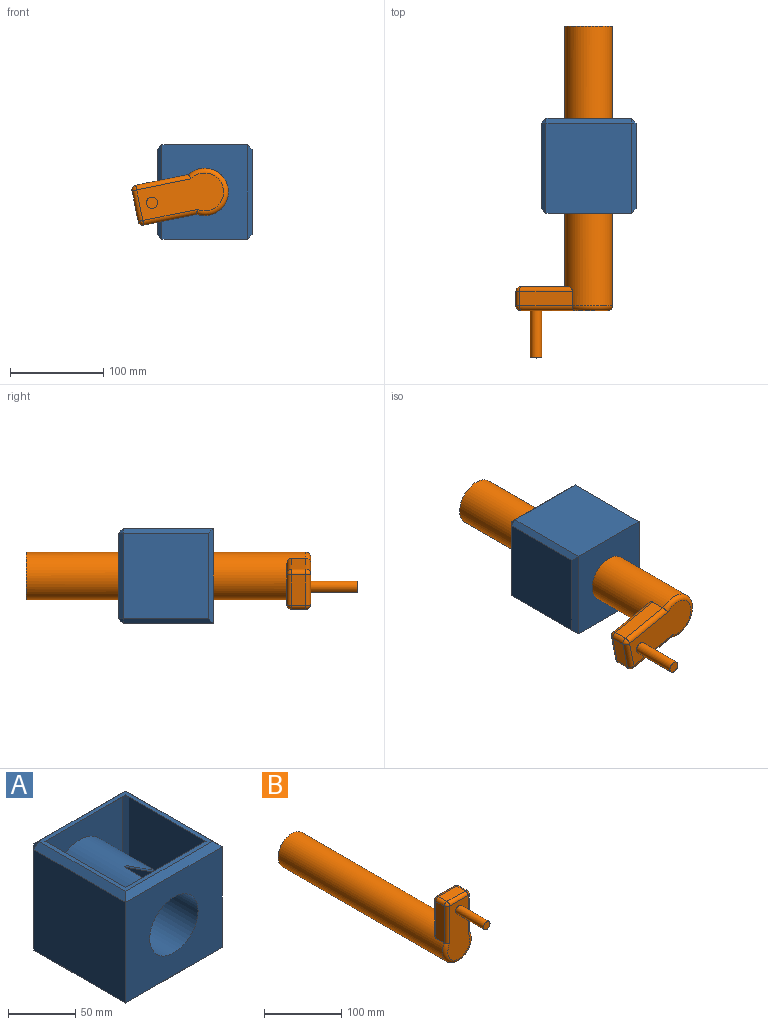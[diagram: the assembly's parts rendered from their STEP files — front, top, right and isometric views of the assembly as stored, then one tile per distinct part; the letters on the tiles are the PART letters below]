
ASSEMBLY  parts=2 mates=1
PART A: 44 faces, bbox 101.6x101.6x101.6 mm
  f0: cylinder r=27.94mm len=96.52mm, axis (0,-1,0), area 16821.6mm2, adj f25,f26,f41,f42,f43
  f1: plane 91.44x91.44mm, normal (0,0,1), area 1262.2mm2, adj f8,f9,f11,f12,f27,f28,f30,f31
  f2: plane 96.52x91.44mm, normal (-1,0,0), area 8825.8mm2, adj f5,f8,f13,f16
  f3: plane 91.44x91.44mm, normal (0,0,-1), area 8361.3mm2, adj f16,f18,f19,f21
  f4: plane 96.52x91.44mm, normal (1,0,0), area 8825.8mm2, adj f5,f11,f17,f21
  f5: plane 101.6x91.44mm, normal (0,-1,0), area 7263.5mm2, adj f2,f4,f7,f9,f19
  f6: plane 91.44x91.44mm, normal (0,1,0), area 6334.4mm2, adj f7,f12,f13,f17,f18
  f7: cylinder r=25.4mm len=101.6mm, axis (0,-1,0), area 16214.6mm2, adj f5,f6
  f8: plane 96.52x5.08mm, normal (-0.71,0,0.71), area 675.2mm2, adj f1,f2,f9,f10
  f9: plane 101.6x5.08mm, normal (0,-0.71,0.71), area 693.4mm2, adj f1,f5,f8,f11
  f10: plane 5.08x5.08mm, normal (-0.58,0.58,0.58), area 22.3mm2, adj f8,f12,f13
  f11: plane 96.52x5.08mm, normal (0.71,0,0.71), area 675.2mm2, adj f1,f4,f9,f14
  f12: plane 91.44x5.08mm, normal (0,0.71,0.71), area 656.9mm2, adj f1,f6,f10,f14
  f13: plane 91.44x5.08mm, normal (-0.71,0.71,0), area 656.9mm2, adj f2,f6,f10,f15
  f14: plane 5.08x5.08mm, normal (0.58,0.58,0.58), area 22.3mm2, adj f11,f12,f17
  f15: plane 5.08x5.08mm, normal (-0.58,0.58,-0.58), area 22.3mm2, adj f13,f16,f18
  f16: plane 96.52x5.08mm, normal (-0.71,0,-0.71), area 675.2mm2, adj f2,f3,f15,f19
  f17: plane 91.44x5.08mm, normal (0.71,0.71,0), area 656.9mm2, adj f4,f6,f14,f20
  f18: plane 91.44x5.08mm, normal (0,0.71,-0.71), area 656.9mm2, adj f3,f6,f15,f20
  f19: plane 101.6x5.08mm, normal (0,-0.71,-0.71), area 693.4mm2, adj f3,f5,f16,f21
  f20: plane 5.08x5.08mm, normal (0.58,0.58,-0.58), area 22.3mm2, adj f17,f18,f21
  f21: plane 96.52x5.08mm, normal (0.71,0,-0.71), area 675.2mm2, adj f3,f4,f19,f20
  f22: plane 92.93x89.34mm, normal (1,0,0), area 8301.8mm2, adj f25,f27,f32,f35
  f23: plane 89.34x89.34mm, normal (0,0,1), area 7980.9mm2, adj f35,f37,f38,f40
  f24: plane 92.93x89.34mm, normal (-1,0,0), area 8301.8mm2, adj f25,f30,f36,f40
  f25: plane 96.52x89.34mm, normal (0,1,0), area 6127.7mm2, adj f0,f22,f24,f28,f38,f41,f42
  f26: plane 89.34x89.34mm, normal (0,-1,0), area 5528.4mm2, adj f0,f31,f32,f36,f37
  f27: plane 93.17x6.13mm, normal (0.71,0,-0.71), area 775.9mm2, adj f1,f22,f28,f29,f31,f32
  f28: plane 96.52x6.13mm, normal (0,0.71,-0.71), area 783.9mm2, adj f1,f25,f27,f30,f43
  f29: plane 3.1x3.1mm, normal (0.58,-0.58,-0.58), area 8.3mm2, adj f27,f31,f32
  f30: plane 93.17x6.13mm, normal (-0.71,0,-0.71), area 775.9mm2, adj f1,f24,f28,f31,f33,f36
  f31: plane 89.83x6.13mm, normal (0,-0.71,-0.71), area 767.9mm2, adj f1,f26,f27,f29,f30,f32,f33,f36
  f32: plane 89.83x3.59mm, normal (0.71,-0.71,0), area 456.1mm2, adj f22,f26,f27,f29,f31,f34,f35,f37
  f33: plane 3.1x3.1mm, normal (-0.58,-0.58,-0.58), area 8.3mm2, adj f30,f31,f36
  f34: plane 3.1x3.1mm, normal (0.58,-0.58,0.58), area 8.3mm2, adj f32,f35,f37
  f35: plane 93.17x3.59mm, normal (0.71,0,0.71), area 464.1mm2, adj f22,f23,f32,f34,f37,f38
  f36: plane 89.83x3.59mm, normal (-0.71,-0.71,0), area 456.1mm2, adj f24,f26,f30,f31,f33,f37,f39,f40
  f37: plane 89.83x3.59mm, normal (0,-0.71,0.71), area 456.1mm2, adj f23,f26,f32,f34,f35,f36,f39,f40
  f38: plane 96.52x3.59mm, normal (0,0.71,0.71), area 472.1mm2, adj f23,f25,f35,f40
  f39: plane 3.1x3.1mm, normal (-0.58,-0.58,0.58), area 8.3mm2, adj f36,f37,f40
  f40: plane 93.17x3.59mm, normal (-0.71,0,0.71), area 464.1mm2, adj f23,f24,f36,f37,f38,f39
  f41: plane 48.34x16.76mm, normal (1,0,0), area 405mm2, adj f0,f25,f43
  f42: plane 48.34x16.76mm, normal (-1,0,0), area 405mm2, adj f0,f25,f43
  f43: plane 48.34x16.76mm, normal (0,0.33,0.94), area 129.8mm2, adj f0,f28,f41,f42
PART B: 22 faces, bbox 55x355.6x103.5 mm
  f0: cylinder r=25.4mm len=299.72mm, axis (0,1,0), area 46788.4mm2, adj f2,f3,f4,f5,f7,f10,f18
  f1: plane 91.29x40.64mm, normal (0,-1,0), area 2961.7mm2, adj f14,f16,f18,f19,f20
  f2: plane 50.8x50.8mm, normal (0,1,0), area 2026.8mm2, adj f0
  f3: plane 57.91x15.24mm, normal (1,0,0), area 882.6mm2, adj f0,f10,f15,f19
  f4: plane 51.84x33.41mm, normal (0,1,0), area 1588.6mm2, adj f0,f7,f9,f10
  f5: plane 57.91x15.24mm, normal (-1,0,0), area 882.6mm2, adj f0,f7,f11,f16
  f6: plane 33.41x15.24mm, normal (0,0,1), area 509.2mm2, adj f9,f11,f14,f15
  f7: cylinder r=5.08mm len=57.91mm, axis (0,0,1), area 442.3mm2, adj f0,f4,f5,f8
  f8: sphere r=5.08mm, area 40.5mm2, adj f7,f9,f11
  f9: cylinder r=5.08mm len=33.41mm, axis (-1,0,0), area 266.6mm2, adj f4,f6,f8,f12
  f10: cylinder r=5.08mm len=57.91mm, axis (0,0,-1), area 442.3mm2, adj f0,f3,f4,f12
  f11: cylinder r=5.08mm len=15.24mm, axis (0,-1,0), area 121.6mm2, adj f5,f6,f8,f13
  f12: sphere r=5.08mm, area 40.5mm2, adj f9,f10,f15
  f13: sphere r=5.08mm, area 40.5mm2, adj f11,f14,f16
  f14: cylinder r=5.08mm len=33.41mm, axis (-1,0,0), area 266.6mm2, adj f1,f6,f13,f17
  f15: cylinder r=5.08mm len=15.24mm, axis (0,1,0), area 121.6mm2, adj f3,f6,f12,f17
  f16: cylinder r=5.08mm len=59.4mm, axis (0,0,1), area 466.3mm2, adj f1,f5,f13,f18
  f17: sphere r=5.08mm, area 40.5mm2, adj f14,f15,f19
  f18: torus R=20.32mm, axis (0,-1,0), area 801.4mm2, adj f0,f1,f16,f19
  f19: cylinder r=5.08mm len=59.4mm, axis (0,0,-1), area 466.3mm2, adj f1,f3,f17,f18
  f20: cylinder r=6.05mm len=50.8mm, axis (0,1,0), area 1930.7mm2, adj f1,f21
  f21: plane 12.1x12.1mm, normal (0,-1,0), area 114.9mm2, adj f20
PLACE A rot(axis=(0,1,0),90deg) t=(0,2.54,50.8)mm
PLACE B rot(axis=(0,-1,0),101.5deg) t=(0,50.8,50.8)mm
MATE revolute B.f0 <-> A.f0  axis (0,1,0) through (0,2.54,50.8)mm
